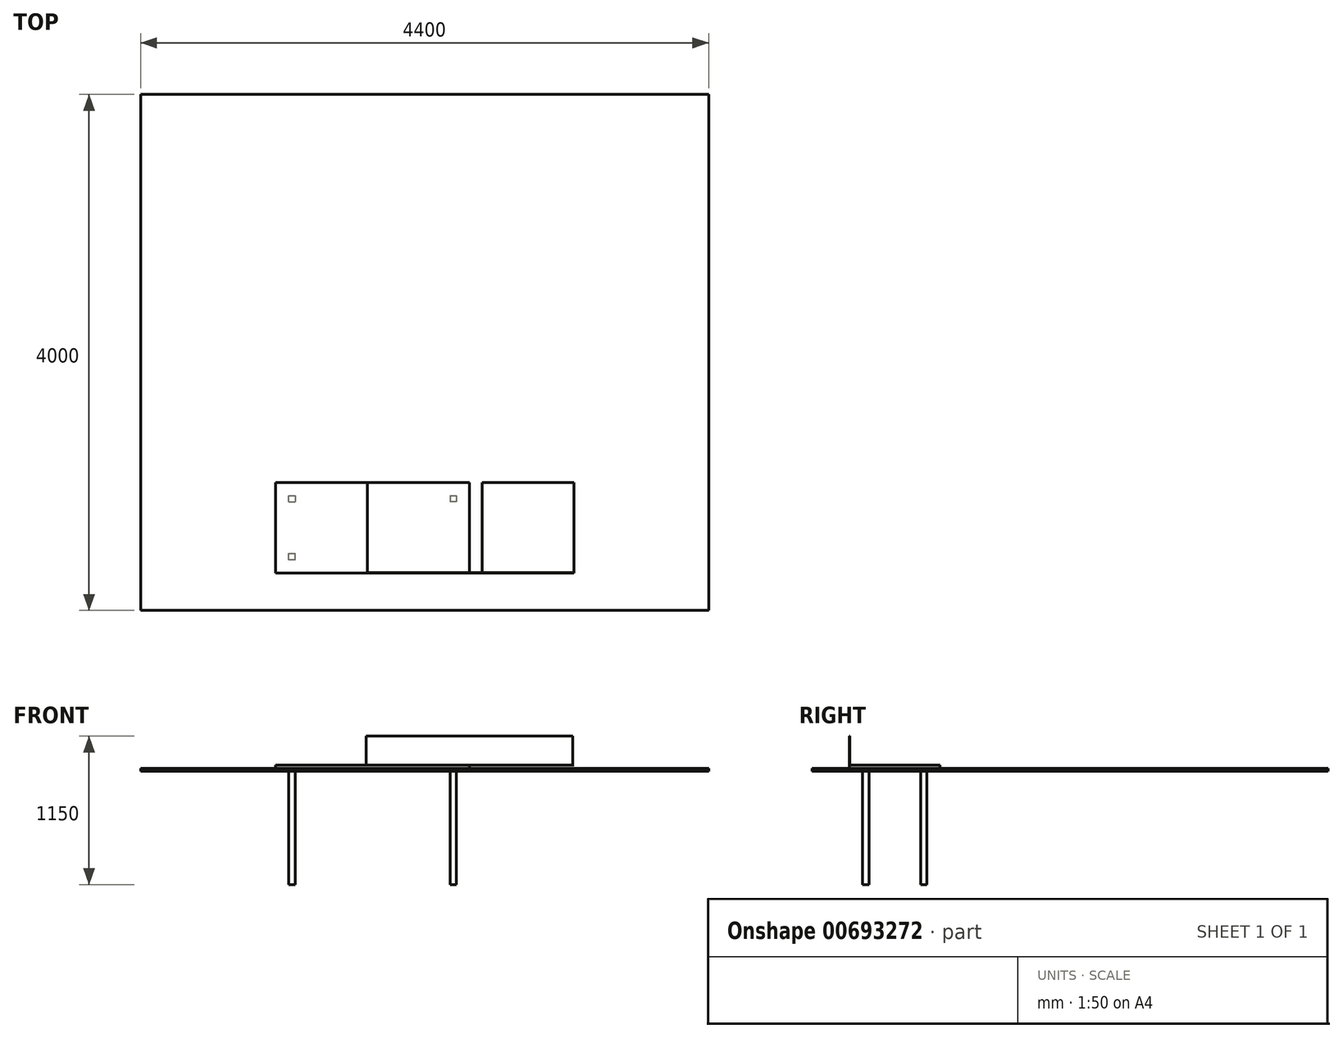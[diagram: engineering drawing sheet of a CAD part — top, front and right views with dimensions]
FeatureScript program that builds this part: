
annotation { "Feature Type Name" : "Feature", "Feature Type Description" : "" }
export const myFeature = defineFeature(function(context is Context, id is Id, definition is map)
    precondition{}
    {
        {
            var Q0;
            Q0=qCreatedBy(makeId("Right.planeOp"),FACE);
            var sketch = newSketch(context, id + "F0", { "sketchPlane" : qUnion([Q0])});
            skLineSegment(sketch, "E0.bottom", {"start": v(657.13, 1522.99) * mm, "end": v(-42.87, 1522.99) * mm});
            skLineSegment(sketch, "E0.top", {"start": v(657.13, 22.99) * mm, "end": v(-42.87, 22.99) * mm});
            skLineSegment(sketch, "E0.left", {"start": v(657.13, 1522.99) * mm, "end": v(657.13, 22.99) * mm});
            skLineSegment(sketch, "E0.right", {"start": v(-42.87, 1522.99) * mm, "end": v(-42.87, 22.99) * mm});
            skSolve(sketch);
        }
        {
            var Q0;
            Q0 = qSketchRegion(id + "F0", true);
            extrude(context, id + "F1", {"entities" : qUnion([Q0]), "depth" : 25 * mm, "offsetDistance" : 25 * mm});
        }
        {
            var Q0;
            Q0=makeQuery(id+"F1.opExtrude","CAP_FACE",FACE,{"disambiguationData":[OSD([sQuery(id+"F0.wireOp",EDGE,"E0.bottom"),sQuery(id+"F0.wireOp",EDGE,"E0.top"),sQuery(id+"F0.wireOp",EDGE,"E0.left"),sQuery(id+"F0.wireOp",EDGE,"E0.right")])],"isStart":true});
            var sketch = newSketch(context, id + "F2", { "sketchPlane" : qUnion([Q0])});
            skLineSegment(sketch, "E1.0", {"start": v(-557.13, 122.99) * mm, "end": v(-57.13, 122.99) * mm});
            skLineSegment(sketch, "E1.1", {"start": v(-557.13, 1422.99) * mm, "end": v(-557.13, 122.99) * mm});
            skLineSegment(sketch, "E1.2", {"start": v(-57.13, 1422.99) * mm, "end": v(-557.13, 1422.99) * mm});
            skLineSegment(sketch, "E1.3", {"start": v(-57.13, 122.99) * mm, "end": v(-57.13, 1422.99) * mm});
            skLineSegment(sketch, "E2.bottom", {"start": v(-57.13, 122.99) * mm, "end": v(-107.13, 122.99) * mm});
            skLineSegment(sketch, "E2.top", {"start": v(-57.13, 172.99) * mm, "end": v(-107.13, 172.99) * mm});
            skLineSegment(sketch, "E2.left", {"start": v(-57.13, 122.99) * mm, "end": v(-57.13, 172.99) * mm});
            skLineSegment(sketch, "E2.right", {"start": v(-107.13, 122.99) * mm, "end": v(-107.13, 172.99) * mm});
            skLineSegment(sketch, "E3.MirrorCS", {"start": v(-57.13, 1372.99) * mm, "end": v(-107.13, 1372.99) * mm});
            skLineSegment(sketch, "E4.MirrorCS", {"start": v(-57.13, 1422.99) * mm, "end": v(-57.13, 1372.99) * mm});
            skLineSegment(sketch, "E5.MirrorCS", {"start": v(-57.13, 1422.99) * mm, "end": v(-107.13, 1422.99) * mm});
            skLineSegment(sketch, "E6.MirrorCS", {"start": v(-107.13, 1422.99) * mm, "end": v(-107.13, 1372.99) * mm});
            skLineSegment(sketch, "E7.MirrorCS", {"start": v(-557.13, 172.99) * mm, "end": v(-507.13, 172.99) * mm});
            skLineSegment(sketch, "E8.MirrorCS", {"start": v(-507.13, 122.99) * mm, "end": v(-507.13, 172.99) * mm});
            skLineSegment(sketch, "E9.MirrorCS", {"start": v(-557.13, 122.99) * mm, "end": v(-557.13, 172.99) * mm});
            skLineSegment(sketch, "E10.MirrorCS", {"start": v(-557.13, 122.99) * mm, "end": v(-507.13, 122.99) * mm});
            skLineSegment(sketch, "E11.MirrorCS", {"start": v(-507.13, 1422.99) * mm, "end": v(-507.13, 1372.99) * mm});
            skLineSegment(sketch, "E12.MirrorCS", {"start": v(-557.13, 1372.99) * mm, "end": v(-507.13, 1372.99) * mm});
            skLineSegment(sketch, "E13.MirrorCS", {"start": v(-557.13, 122.99) * mm, "end": v(-557.13, 1422.99) * mm});
            skLineSegment(sketch, "E14.MirrorCS", {"start": v(-557.13, 1422.99) * mm, "end": v(-57.13, 1422.99) * mm});
            skSolve(sketch);
        }
        {
            var Q0;
            Q0=makeQuery(id+"F2.imprint","IMPRINT",FACE,{"disambiguationData":[TD([[makeQuery(id+"F2.imprint","IMPRINT",EDGE,{"derivedFrom":sQuery(id+"F2.wireOp",EDGE,"E3.MirrorCS")}),-1.0]])]});
            var Q1;
            {var subQ0=sQuery(id+"F2.wireOp",EDGE,"E11.MirrorCS");Q1=makeQuery(id+"F2.imprint","IMPRINT",FACE,{"disambiguationData":[TD([[makeQuery(id+"F2.imprint","IMPRINT",EDGE,{"derivedFrom":subQ0}),-1.0]])]});}
            var Q2;
            Q2=makeQuery(id+"F2.imprint","IMPRINT",FACE,{"disambiguationData":[TD([[makeQuery(id+"F2.imprint","IMPRINT",EDGE,{"derivedFrom":sQuery(id+"F2.wireOp",EDGE,"E2.bottom")}),-1.0]])]});
            var Q3;
            {var subQ0=sQuery(id+"F2.wireOp",EDGE,"E7.MirrorCS");Q3=makeQuery(id+"F2.imprint","IMPRINT",FACE,{"disambiguationData":[TD([[makeQuery(id+"F2.imprint","IMPRINT",EDGE,{"derivedFrom":subQ0}),-1.0]])]});}
            extrude(context, id + "F3", {"entities" : qUnion([Q0, Q1, Q2, Q3]), "operationType" : NewBodyOperationType.ADD, "depth" : 900 * mm, "offsetDistance" : 25 * mm});
        }
        {
            var Q0;
            Q0=makeQuery(id+"F1.opExtrude","SWEPT_BODY",BODY,{"disambiguationData":[OSD([sQuery(id+"F0.wireOp",EDGE,"E0.bottom"),sQuery(id+"F0.wireOp",EDGE,"E0.top"),sQuery(id+"F0.wireOp",EDGE,"E0.left"),sQuery(id+"F0.wireOp",EDGE,"E0.right")])]});
            var Q1;
            Q1=makeQuery(id+"F1.opExtrude","CAP_EDGE",EDGE,{"disambiguationData":[OSD([sQuery(id+"F0.wireOp",EDGE,"E0.top")])],"isStart":true});
            transform(context, id + "F4", {"entities" : qUnion([Q0]), "transformType" : TransformType.ROTATION, "transformAxis" : qUnion([Q1]), "angle" : 90 * degree, "makeCopy" : false});
        }
        {
            var Q0;
            Q0=qCreatedBy(makeId("Top.planeOp"),FACE);
            var sketch = newSketch(context, id + "F5", { "sketchPlane" : qUnion([Q0])});
            skLineSegment(sketch, "E15.bottom", {"start": v(-2546.45, 3666) * mm, "end": v(1853.55, 3666) * mm});
            skLineSegment(sketch, "E15.top", {"start": v(-2546.45, -334) * mm, "end": v(1853.55, -334) * mm});
            skLineSegment(sketch, "E15.left", {"start": v(-2546.45, 3666) * mm, "end": v(-2546.45, -334) * mm});
            skLineSegment(sketch, "E15.right", {"start": v(1853.55, 3666) * mm, "end": v(1853.55, -334) * mm});
            skSolve(sketch);
        }
        {
            var Q0;
            Q0 = qSketchRegion(id + "F5", true);
            extrude(context, id + "F6", {"entities" : qUnion([Q0]), "depth" : 25 * mm, "offsetDistance" : 25 * mm});
        }
        {
            var Q0;
            Q0=makeQuery(id+"F1.opExtrude","CAP_FACE",FACE,{"disambiguationData":[OSD([sQuery(id+"F0.wireOp",EDGE,"E0.bottom"),sQuery(id+"F0.wireOp",EDGE,"E0.top"),sQuery(id+"F0.wireOp",EDGE,"E0.left"),sQuery(id+"F0.wireOp",EDGE,"E0.right")])],"isStart":false});
            var sketch = newSketch(context, id + "F7", { "sketchPlane" : qUnion([Q0])});
            skLineSegment(sketch, "E16", {"start": v(-1500, -42.87) * mm, "end": v(-800, -42.87) * mm});
            skLineSegment(sketch, "E17", {"start": v(-800, -42.87) * mm, "end": v(800, -42.87) * mm});
            skLineSegment(sketch, "E18", {"start": v(800, -42.87) * mm, "end": v(800, -39.87) * mm});
            skLineSegment(sketch, "E19", {"start": v(800, -39.87) * mm, "end": v(-800, -39.87) * mm});
            skLineSegment(sketch, "E20", {"start": v(-800, -39.87) * mm, "end": v(-800, -42.87) * mm});
            skSolve(sketch);
        }
        {
            var Q0;
            Q0 = qSketchRegion(id + "F7", true);
            extrude(context, id + "F8", {"entities" : qUnion([Q0]), "depth" : 225 * mm, "offsetDistance" : 25 * mm});
        }
        {
            var Q0;
            Q0=makeQuery(id+"F1.opExtrude","CAP_FACE",FACE,{"disambiguationData":[OSD([sQuery(id+"F0.wireOp",EDGE,"E0.bottom"),sQuery(id+"F0.wireOp",EDGE,"E0.top"),sQuery(id+"F0.wireOp",EDGE,"E0.left"),sQuery(id+"F0.wireOp",EDGE,"E0.right")])],"isStart":false});
            var sketch = newSketch(context, id + "F9", { "sketchPlane" : qUnion([Q0])});
            skLineSegment(sketch, "E21.bottom", {"start": v(-1500, 657.13) * mm, "end": v(-791.48, 657.13) * mm});
            skLineSegment(sketch, "E21.top", {"start": v(-1500, -42.87) * mm, "end": v(-791.48, -42.87) * mm});
            skLineSegment(sketch, "E21.left", {"start": v(-1500, 657.13) * mm, "end": v(-1500, -42.87) * mm});
            skLineSegment(sketch, "E21.right", {"start": v(-791.48, 657.13) * mm, "end": v(-791.48, -42.87) * mm});
            skSolve(sketch);
        }
        {
            var Q0;
            Q0 = qSketchRegion(id + "F9", true);
            extrude(context, id + "F10", {"entities" : qUnion([Q0]), "depth" : 1 * mm, "offsetDistance" : 25 * mm});
        }
        {
            var Q0;
            Q0=makeQuery(id+"F10.opExtrude","SWEPT_BODY",BODY,{"disambiguationData":[OSD([sQuery(id+"F9.wireOp",EDGE,"E21.bottom"),sQuery(id+"F9.wireOp",EDGE,"E21.top"),sQuery(id+"F9.wireOp",EDGE,"E21.left"),sQuery(id+"F9.wireOp",EDGE,"E21.right")])]});
            var Q1;
            Q1=makeQuery(id+"F8.opExtrude","CAP_VERTEX",VERTEX,{"disambiguationData":[OSD([sQuery(id+"F7.wireOp",EDGE,"E16"),sQuery(id+"F7.wireOp",EDGE,"E17"),sQuery(id+"F7.wireOp",EDGE,"E20")])],"isStart":false});
            var Q2;
            Q2=makeQuery(id+"F8.opExtrude","CAP_VERTEX",VERTEX,{"disambiguationData":[OSD([sQuery(id+"F7.wireOp",EDGE,"E17"),sQuery(id+"F7.wireOp",EDGE,"E18")])],"isStart":false});
            transform(context, id + "F11", {"entities" : qUnion([Q0]), "transformType" : TransformType.TRANSLATION_ENTITY, "oppositeDirectionEntity" : false, "transformLine" : qUnion([Q1, Q2]), "makeCopy" : true});
        }
    });
